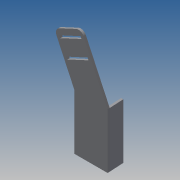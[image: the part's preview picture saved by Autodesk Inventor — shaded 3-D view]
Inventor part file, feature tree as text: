
AUTODESK INVENTOR PART (.ipt)
format: ipt  version: 2013 (Build 170138000, 138)  size: 124,416 bytes
history: native  units: mm
features: extrude x3, sketch x3, pattern_linear x1, fillet x1
ambient origin geometry x8: Origin, YZ Plane, XZ Plane, XY Plane, X Axis, Y Axis, Z Axis, Center Point
bodies: Solid1 (feature_tree)
feature tree (8):
  extrude  "Extrusion1"  Depth=2.0mm
  extrude  "Extrusion2"  Depth=13.0mm
  extrude  "Extrusion3"  Depth=4.363323mm
  pattern_linear  "Rectangular Pattern1"  Count1=5  [1 undecoded]
  fillet  "Fillet1"  Radius=35.0mm
  sketch  "Sketch1"  dims[d0=24.5mm d2=2.0mm]
  sketch  "Sketch2"  dims[d4=26.0mm d5=13.0mm]
  sketch  "Sketch3"  dims[d6=50.0mm d7=0.0mm d8=4.363323mm d13=50.0mm d15=35.0mm d16=0.0mm d17=21.0mm d19=5.0mm d20=2.0mm d21=35.0mm d22=0.0mm d23=20.0mm d25=15.0mm d26=5.0mm d27=2.0mm d28=2.0mm]
note: 1 required parameter value undecoded (feature->parameter linkage not recoverable at this tier; creation-order binding heuristic only, values carry confidence <= 0.55)
